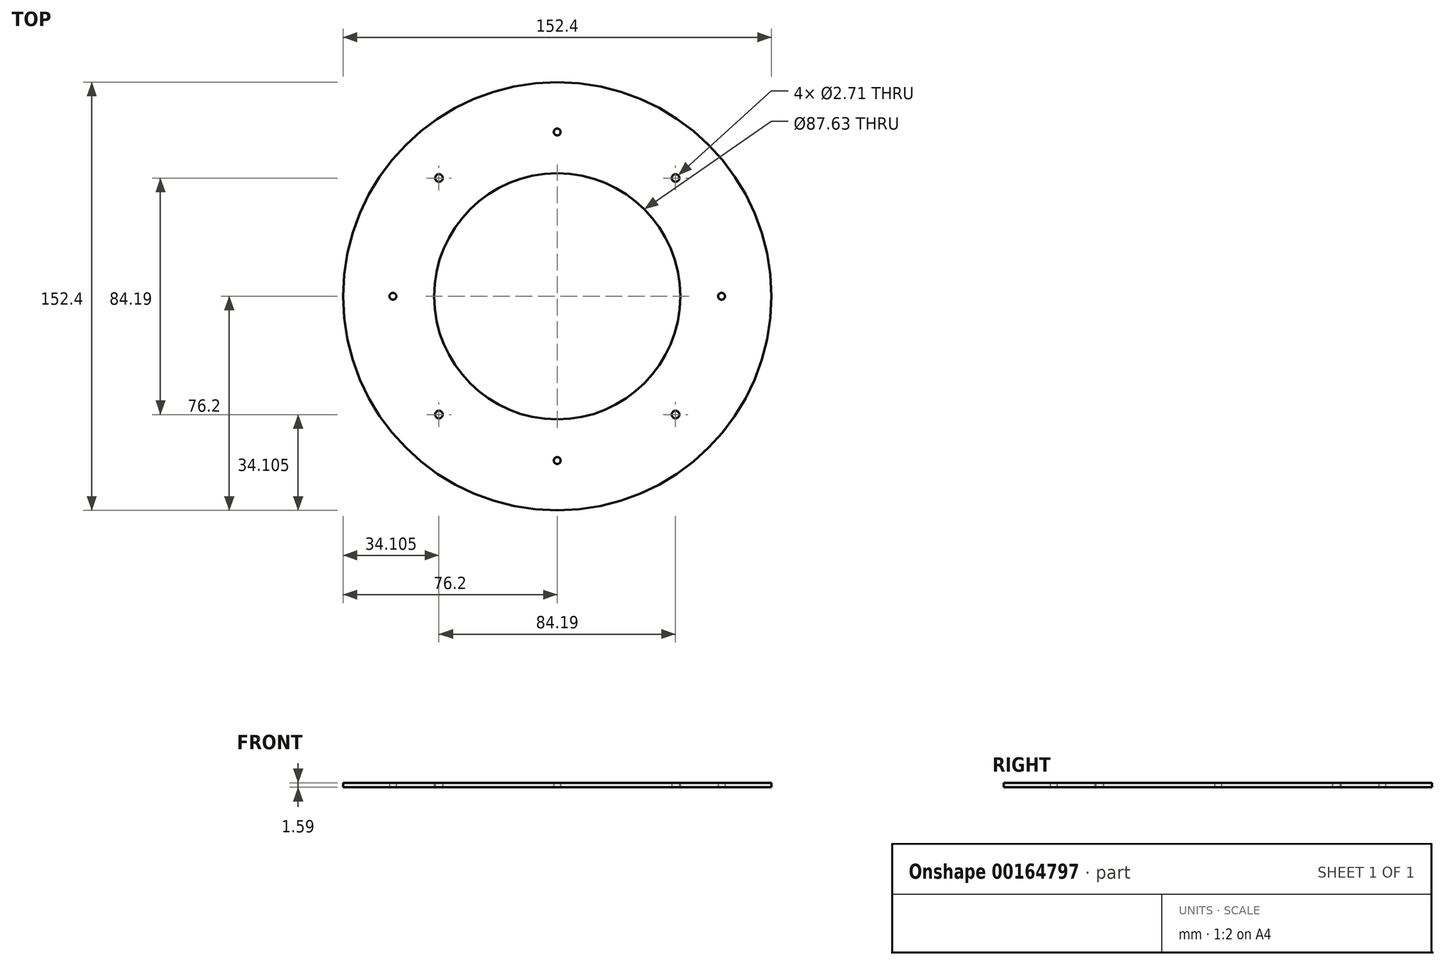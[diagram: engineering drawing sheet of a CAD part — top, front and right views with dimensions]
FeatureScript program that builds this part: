
annotation { "Feature Type Name" : "Feature", "Feature Type Description" : "" }
export const myFeature = defineFeature(function(context is Context, id is Id, definition is map)
    precondition{}
    {
        {
            var Q0;
            Q0=qCreatedBy(makeId("Top.planeOp"),FACE);
            var sketch = newSketch(context, id + "F0", { "sketchPlane" : qUnion([Q0])});
            skLineSegment(sketch, "E0.bottom", {"start": v(58.47, 0) * mm, "end": v(0, 58.47) * mm, "construction": true});
            skLineSegment(sketch, "E0.top", {"start": v(0, -58.47) * mm, "end": v(-58.47, 0) * mm, "construction": true});
            skLineSegment(sketch, "E0.left", {"start": v(58.47, 0) * mm, "end": v(0, -58.47) * mm, "construction": true});
            skLineSegment(sketch, "E0.right", {"start": v(0, 58.47) * mm, "end": v(-58.47, 0) * mm, "construction": true});
            skPoint(sketch, "E0.middle", {"position": v(0, 0) * mm});
            skCircle(sketch, "E1", {"center": v(0, 0) * mm, "radius": 43.82 * mm});
            skCircle(sketch, "E2", {"center": v(58.47, 0) * mm, "radius": 1.22 * mm});
            skCircle(sketch, "E3", {"center": v(0, 58.47) * mm, "radius": 1.22 * mm});
            skCircle(sketch, "E4", {"center": v(-58.47, 0) * mm, "radius": 1.22 * mm});
            skCircle(sketch, "E5", {"center": v(0, -58.47) * mm, "radius": 1.22 * mm});
            skCircle(sketch, "E6", {"center": v(0, 0) * mm, "radius": 76.2 * mm});
            skLineSegment(sketch, "E7.bottom", {"start": v(-42.1, 42.1) * mm, "end": v(-42.1, -42.1) * mm, "construction": true});
            skLineSegment(sketch, "E7.top", {"start": v(42.1, 42.1) * mm, "end": v(42.1, -42.1) * mm, "construction": true});
            skLineSegment(sketch, "E7.left", {"start": v(-42.1, 42.1) * mm, "end": v(42.1, 42.1) * mm, "construction": true});
            skLineSegment(sketch, "E7.right", {"start": v(-42.1, -42.1) * mm, "end": v(42.1, -42.1) * mm, "construction": true});
            skCircle(sketch, "E8", {"center": v(-42.1, 42.1) * mm, "radius": 3.97 * mm, "construction": true});
            skCircle(sketch, "E9", {"center": v(-42.1, -42.1) * mm, "radius": 1.35 * mm});
            skCircle(sketch, "E10", {"center": v(-42.1, 42.1) * mm, "radius": 1.35 * mm});
            skCircle(sketch, "E11", {"center": v(42.1, 42.1) * mm, "radius": 1.35 * mm});
            skCircle(sketch, "E12", {"center": v(42.1, -42.1) * mm, "radius": 1.35 * mm});
            skCircle(sketch, "E13", {"center": v(0, 0) * mm, "radius": 63.5 * mm, "construction": true});
            skLineSegment(sketch, "E14", {"start": v(0, -58.47) * mm, "end": v(0, 0) * mm, "construction": true});
            skSolve(sketch);
        }
        {
            var Q0;
            Q0=makeQuery(id+"F0.imprint","IMPRINT",FACE,{"disambiguationData":[TD([[makeQuery(id+"F0.imprint","IMPRINT",EDGE,{"derivedFrom":sQuery(id+"F0.wireOp",EDGE,"E1")}),-1.0]])]});
            extrude(context, id + "F1", {"entities" : qUnion([Q0]), "depth" : 1.59 * mm});
        }
    });
